# Revit family: Desk-Teknion-CTDP_Table_Desk_Angled_Leg_With_Single_Pedestal-R2021
name_source: partatom
category: Furniture
units: mm (PartAtom-declared; Revit-internal decimal feet)

## family parameters
Always vertical = Yes
Cut with Voids When Loaded = No
OmniClass Number = 23.40.20.00
OmniClass Title = General Furniture and Specialties
Room Calculation Point = No
Shared = Yes
Work Plane-Based = No

## types (4) — shared parameters
Assembly Code = E2020200
Manufacturer = Teknion
Manufacturer Fax = 416.661.4586
Model = CTDP__A__
Part Number = CTDP
Product Documentation Link = https://www.teknion.com
Product Line = Chronicle
Product Page URL = https://www.teknion.com
Series = Chronicle
Sustainability Data = https://www.teknion.com
URL = www.teknion.com
Unit Weight URL = http://www.teknion.com
Warranty = http://www.teknion.com
zero-valued in all types: Default Elevation

## per-type parameters (varying)
| type | 2 Box, 1 File | 2 File | Cut-Out - Front 1 | Description | Pedestal Size |
| 18", 2 Box, 1 File Pedestal | Yes | No | 5 " | Table Desk, Angled Leg With Single Pedestal, Partial Height & Inset Modesty, 18" BBF Pedestal Type | 18 " |
| 15", 2 Box, 1 File Pedestal | Yes | No | 5 " | Table Desk, Angled Leg With Single Pedestal, Partial Height & Inset Modesty, 15" BBF Pedestal Type | 15.5 " |
| 15", 2 File Pedestal | No | Yes | 1 " | Table Desk, Angled Leg With Single Pedestal, Partial Height & Inset Modesty, 15" FF Pedestal Type | 15.5 " |
| 18", 2 File Pedestal | No | Yes | 1 " | Table Desk, Angled Leg With Single Pedestal, Partial Height & Inset Modesty, 18" FF Pedestal Type | 18 " |

## geometry (parser evidence)
native form markers: Sweep x3
no freeform markers — native parametric forms only
